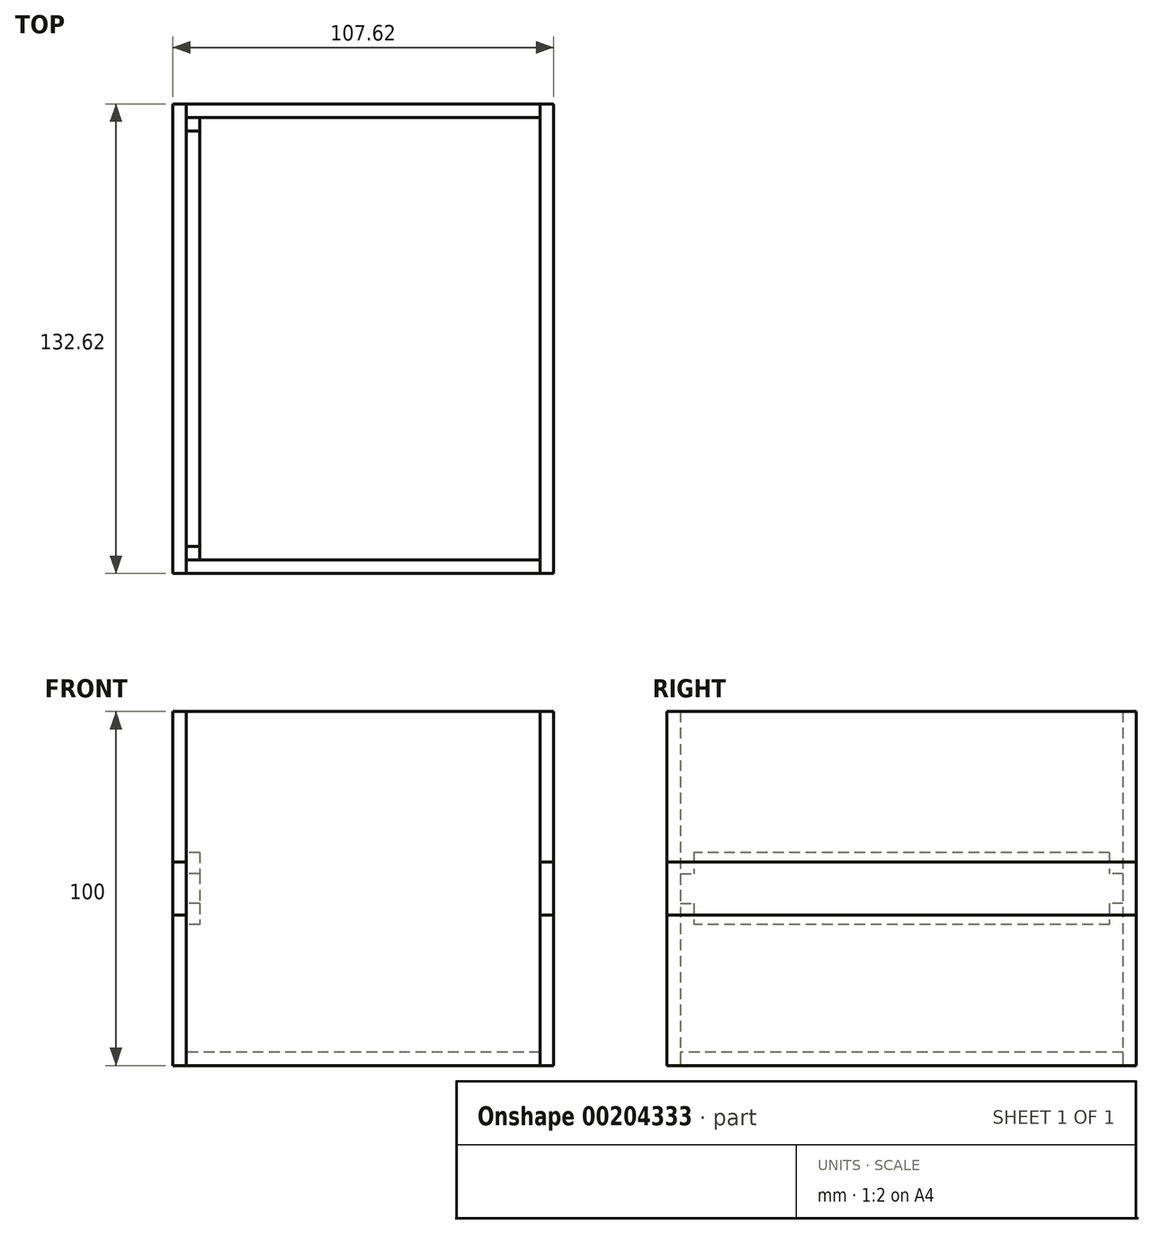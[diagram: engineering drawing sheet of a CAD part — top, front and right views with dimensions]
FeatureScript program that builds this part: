
annotation { "Feature Type Name" : "Feature", "Feature Type Description" : "" }
export const myFeature = defineFeature(function(context is Context, id is Id, definition is map)
    precondition{}
    {
        {
            var Q0;
            Q0=qCreatedBy(makeId("Top.planeOp"),FACE);
            var sketch = newSketch(context, id + "F0", { "sketchPlane" : qUnion([Q0])});
            skLineSegment(sketch, "E0.bottom", {"start": v(50, 62.5) * mm, "end": v(-50, 62.5) * mm});
            skLineSegment(sketch, "E0.top", {"start": v(50, -62.5) * mm, "end": v(-50, -62.5) * mm});
            skLineSegment(sketch, "E0.left", {"start": v(50, 62.5) * mm, "end": v(50, -62.5) * mm});
            skLineSegment(sketch, "E0.right", {"start": v(-50, 62.5) * mm, "end": v(-50, -62.5) * mm});
            skPoint(sketch, "E0.middle", {"position": v(0, 0) * mm});
            skSolve(sketch);
        }
        {
            var Q0;
            Q0=makeQuery(id+"F0.imprint","IMPRINT",FACE,{"disambiguationData":[TD([[makeQuery(id+"F0.imprint","IMPRINT",EDGE,{"derivedFrom":sQuery(id+"F0.wireOp",EDGE,"E0.bottom")}),1.0]])]});
            extrude(context, id + "F1", {"entities" : qUnion([Q0]), "depth" : 3.8 * mm});
        }
        {
            var Q0;
            Q0=qCreatedBy(makeId("Top.planeOp"),FACE);
            var sketch = newSketch(context, id + "F2", { "sketchPlane" : qUnion([Q0])});
            skLineSegment(sketch, "E1.bottom", {"start": v(-50, 62.5) * mm, "end": v(50, 62.5) * mm});
            skLineSegment(sketch, "E1.top", {"start": v(-50, 66.3) * mm, "end": v(50, 66.3) * mm});
            skLineSegment(sketch, "E1.left", {"start": v(-50, 62.5) * mm, "end": v(-50, 66.3) * mm});
            skLineSegment(sketch, "E1.right", {"start": v(50, 62.5) * mm, "end": v(50, 66.3) * mm});
            skLineSegment(sketch, "E2.MirrorCS", {"start": v(50, -62.5) * mm, "end": v(50, -66.3) * mm});
            skLineSegment(sketch, "E3.MirrorCS", {"start": v(-50, -62.5) * mm, "end": v(-50, -66.3) * mm});
            skLineSegment(sketch, "E4.MirrorCS", {"start": v(-50, -62.5) * mm, "end": v(50, -62.5) * mm});
            skLineSegment(sketch, "E5.MirrorCS", {"start": v(-50, -66.3) * mm, "end": v(50, -66.3) * mm});
            skSolve(sketch);
        }
        {
            var Q0;
            Q0 = qSketchRegion(id + "F2", true);
            extrude(context, id + "F3", {"entities" : qUnion([Q0]), "depth" : 100 * mm});
        }
        {
            var Q0;
            Q0=qCreatedBy(makeId("Top.planeOp"),FACE);
            var sketch = newSketch(context, id + "F4", { "sketchPlane" : qUnion([Q0])});
            skPoint(sketch, "E6.0", {"position": v(-50, 66.3) * mm});
            skLineSegment(sketch, "E7.bottom", {"start": v(-50, 66.3) * mm, "end": v(-53.8, 66.3) * mm});
            skLineSegment(sketch, "E7.top", {"start": v(-50, -66.3) * mm, "end": v(-53.8, -66.3) * mm});
            skLineSegment(sketch, "E7.left", {"start": v(-50, 66.3) * mm, "end": v(-50, -66.3) * mm});
            skLineSegment(sketch, "E7.right", {"start": v(-53.8, 66.3) * mm, "end": v(-53.8, -66.3) * mm});
            skLineSegment(sketch, "E8.MirrorCS", {"start": v(50, 66.3) * mm, "end": v(53.8, 66.3) * mm});
            skLineSegment(sketch, "E9.MirrorCS", {"start": v(50, -66.3) * mm, "end": v(53.8, -66.3) * mm});
            skLineSegment(sketch, "E10.MirrorCS", {"start": v(53.8, 66.3) * mm, "end": v(53.8, -66.3) * mm});
            skLineSegment(sketch, "E11.MirrorCS", {"start": v(50, 66.3) * mm, "end": v(50, -66.3) * mm});
            skPoint(sketch, "E12.MirrorP", {"position": v(50, 66.3) * mm});
            skSolve(sketch);
        }
        {
            var Q0;
            Q0 = qSketchRegion(id + "F4", true);
            var Q1;
            Q1=makeQuery(id+"F3.opExtrude","CAP_FACE",FACE,{"disambiguationData":[OSD([sQuery(id+"F2.wireOp",EDGE,"E1.bottom"),sQuery(id+"F2.wireOp",EDGE,"E1.top"),sQuery(id+"F2.wireOp",EDGE,"E1.left"),sQuery(id+"F2.wireOp",EDGE,"E1.right")])],"isStart":false});
            extrude(context, id + "F5", {"entities" : qUnion([Q0]), "endBound" : BoundingType.UP_TO_SURFACE, "endBoundEntityFace" : qUnion([Q1]), "depth" : 25 * mm});
        }
        {
            var Q0;
            Q0=makeQuery(id+"F5.opExtrude","SWEPT_FACE",FACE,{"disambiguationData":[OSD([sQuery(id+"F4.wireOp",EDGE,"E7.right")])]});
            var sketch = newSketch(context, id + "F6", { "sketchPlane" : qUnion([Q0])});
            skLineSegment(sketch, "E13", {"start": v(-66.3, 50) * mm, "end": v(66.3, 50) * mm, "construction": true});
            skLineSegment(sketch, "E14.bottom", {"start": v(66.3, 57.5) * mm, "end": v(-66.3, 57.5) * mm});
            skLineSegment(sketch, "E14.top", {"start": v(66.3, 42.5) * mm, "end": v(-66.3, 42.5) * mm});
            skLineSegment(sketch, "E14.left", {"start": v(66.3, 57.5) * mm, "end": v(66.3, 42.5) * mm});
            skLineSegment(sketch, "E14.right", {"start": v(-66.3, 57.5) * mm, "end": v(-66.3, 42.5) * mm});
            skPoint(sketch, "E14.middle", {"position": v(0, 50) * mm});
            skLineSegment(sketch, "E15.MirrorCS", {"start": v(-66.3, 42.5) * mm, "end": v(-66.3, 57.5) * mm});
            skLineSegment(sketch, "E16.MirrorCS", {"start": v(66.3, 42.5) * mm, "end": v(66.3, 57.5) * mm});
            skSolve(sketch);
        }
        {
            var Q0;
            Q0 = qSketchRegion(id + "F6", true);
            var Q1;
            Q1=makeQuery(id+"F5.opExtrude","SWEPT_FACE",FACE,{"disambiguationData":[OSD([sQuery(id+"F4.wireOp",EDGE,"E7.left")])]});
            extrude(context, id + "F7", {"entities" : qUnion([Q0]), "endBound" : BoundingType.UP_TO_SURFACE, "oppositeDirection" : true, "endBoundEntityFace" : qUnion([Q1]), "depth" : 25 * mm});
        }
        {
            var Q0;
            Q0=makeQuery(id+"F7.opExtrude","SWEPT_BODY",BODY,{"disambiguationData":[OSD([sQuery(id+"F6.wireOp",EDGE,"E14.right"),sQuery(id+"F6.wireOp",EDGE,"E14.left"),sQuery(id+"F6.wireOp",EDGE,"E14.bottom"),sQuery(id+"F6.wireOp",EDGE,"E14.top")])]});
            var Q1;
            Q1=qCreatedBy(makeId("Right.planeOp"),FACE);
            mirror(context, id + "F8", {"entities" : qUnion([Q0]), "mirrorPlane" : qUnion([Q1])});
        }
        {
            var Q0;
            Q0=makeQuery(id+"F8.opPattern","COPY",BODY,{"derivedFrom":makeQuery(id+"F7.opExtrude","SWEPT_BODY",BODY,{"disambiguationData":[OSD([sQuery(id+"F6.wireOp",EDGE,"E14.right"),sQuery(id+"F6.wireOp",EDGE,"E14.left"),sQuery(id+"F6.wireOp",EDGE,"E14.bottom"),sQuery(id+"F6.wireOp",EDGE,"E14.top")])]}),"instanceName":"1"});
            var Q1;
            Q1=makeQuery(id+"F7.opExtrude","SWEPT_BODY",BODY,{"disambiguationData":[OSD([sQuery(id+"F6.wireOp",EDGE,"E14.right"),sQuery(id+"F6.wireOp",EDGE,"E14.left"),sQuery(id+"F6.wireOp",EDGE,"E14.bottom"),sQuery(id+"F6.wireOp",EDGE,"E14.top")])]});
            var Q2;
            Q2=makeQuery(id+"F5.opExtrude","SWEPT_BODY",BODY,{"disambiguationData":[OSD([sQuery(id+"F4.wireOp",EDGE,"E7.bottom"),sQuery(id+"F4.wireOp",EDGE,"E7.top"),sQuery(id+"F4.wireOp",EDGE,"E7.left"),sQuery(id+"F4.wireOp",EDGE,"E7.right")])]});
            var Q3;
            Q3=makeQuery(id+"F5.opExtrude","SWEPT_BODY",BODY,{"disambiguationData":[OSD([sQuery(id+"F4.wireOp",EDGE,"E8.MirrorCS"),sQuery(id+"F4.wireOp",EDGE,"E9.MirrorCS"),sQuery(id+"F4.wireOp",EDGE,"E10.MirrorCS"),sQuery(id+"F4.wireOp",EDGE,"E11.MirrorCS")])]});
            booleanBodies(context, id + "F9", {"operationType" : BooleanOperationType.SUBTRACTION, "tools" : qUnion([Q0, Q1]), "targets" : qUnion([Q2, Q3]), "keepTools" : true});
        }
        {
            var Q0;
            Q0=makeQuery(id+"F7.opExtrude","CAP_FACE",FACE,{"disambiguationData":[OSD([sQuery(id+"F6.wireOp",EDGE,"E14.right"),sQuery(id+"F6.wireOp",EDGE,"E14.left"),sQuery(id+"F6.wireOp",EDGE,"E14.bottom"),sQuery(id+"F6.wireOp",EDGE,"E14.top")])],"isStart":false});
            var sketch = newSketch(context, id + "F10", { "sketchPlane" : qUnion([Q0])});
            skLineSegment(sketch, "E17", {"start": v(-66.3, 50) * mm, "end": v(66.3, 50) * mm, "construction": true});
            skLineSegment(sketch, "E18.bottom", {"start": v(58.69, 60.17) * mm, "end": v(-58.69, 60.17) * mm});
            skLineSegment(sketch, "E18.top", {"start": v(58.69, 39.83) * mm, "end": v(-58.69, 39.83) * mm});
            skLineSegment(sketch, "E18.left", {"start": v(58.69, 60.17) * mm, "end": v(58.69, 54.2) * mm});
            skLineSegment(sketch, "E18.right", {"start": v(-58.69, 60.17) * mm, "end": v(-58.69, 54.2) * mm});
            skPoint(sketch, "E18.middle", {"position": v(0, 50) * mm});
            skLineSegment(sketch, "E19.bottom", {"start": v(-62.5, 54.2) * mm, "end": v(-58.69, 54.2) * mm});
            skLineSegment(sketch, "E19.top", {"start": v(-62.5, 45.8) * mm, "end": v(-58.69, 45.8) * mm});
            skLineSegment(sketch, "E19.left", {"start": v(-62.5, 54.2) * mm, "end": v(-62.5, 45.8) * mm});
            skPoint(sketch, "E19.middle", {"position": v(-58.69, 50) * mm});
            skLineSegment(sketch, "E20.MirrorCS", {"start": v(62.5, 45.8) * mm, "end": v(58.69, 45.8) * mm});
            skLineSegment(sketch, "E21.MirrorCS", {"start": v(62.5, 54.2) * mm, "end": v(58.69, 54.2) * mm});
            skLineSegment(sketch, "E22.MirrorCS", {"start": v(62.5, 54.2) * mm, "end": v(62.5, 45.8) * mm});
            skLineSegment(sketch, "E23.trimOffspring", {"start": v(-58.69, 45.8) * mm, "end": v(-58.69, 39.83) * mm});
            skLineSegment(sketch, "E24.trimOffspring", {"start": v(58.69, 45.8) * mm, "end": v(58.69, 39.83) * mm});
            skSolve(sketch);
        }
        {
            var Q0;
            Q0 = qSketchRegion(id + "F10", true);
            extrude(context, id + "F11", {"entities" : qUnion([Q0]), "depth" : 3.8 * mm});
        }
    });
